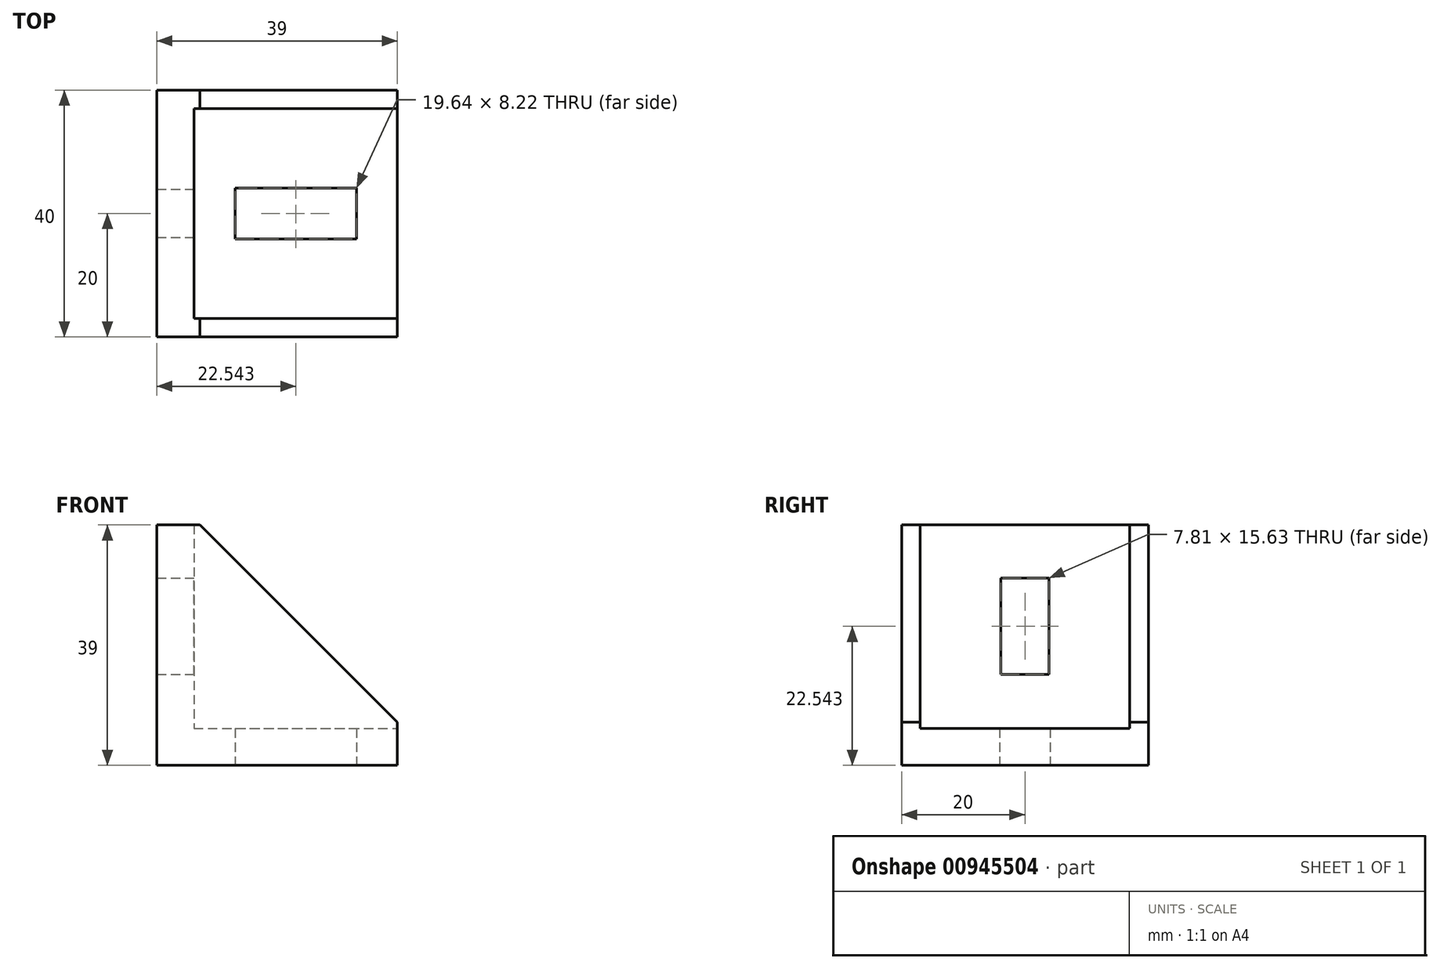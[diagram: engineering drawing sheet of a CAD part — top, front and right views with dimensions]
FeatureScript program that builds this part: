
annotation { "Feature Type Name" : "Feature", "Feature Type Description" : "" }
export const myFeature = defineFeature(function(context is Context, id is Id, definition is map)
    precondition{}
    {
        {
            var Q0;
            Q0=qCreatedBy(makeId("Front.planeOp"),FACE);
            var sketch = newSketch(context, id + "F0", { "sketchPlane" : qUnion([Q0])});
            skLineSegment(sketch, "E0.bottom", {"start": v(0, 0) * mm, "end": v(39, 0) * mm});
            skLineSegment(sketch, "E0.top", {"start": v(0, 39) * mm, "end": v(7, 39) * mm});
            skLineSegment(sketch, "E0.left", {"start": v(0, 0) * mm, "end": v(0, 39) * mm});
            skLineSegment(sketch, "E0.right", {"start": v(39, 0) * mm, "end": v(39, 7) * mm});
            skLineSegment(sketch, "E1", {"start": v(7, 39) * mm, "end": v(39, 7) * mm});
            skSolve(sketch);
        }
        {
            var Q0;
            Q0=makeQuery(id+"F0.imprint","IMPRINT",FACE,{"disambiguationData":[TD([[makeQuery(id+"F0.imprint","IMPRINT",EDGE,{"derivedFrom":sQuery(id+"F0.wireOp",EDGE,"E0.bottom")}),1.0]])]});
            extrude(context, id + "F1", {"entities" : qUnion([Q0]), "endBound" : BoundingType.SYMMETRIC, "depth" : 40 * mm, "offsetDistance" : 25 * mm});
        }
        {
            var Q0;
            Q0=qCreatedBy(makeId("Top.planeOp"),FACE);
            var sketch = newSketch(context, id + "F2", { "sketchPlane" : qUnion([Q0])});
            skLineSegment(sketch, "E2.bottom", {"start": v(6, 17) * mm, "end": v(39, 17) * mm});
            skLineSegment(sketch, "E2.top", {"start": v(6, -17) * mm, "end": v(39, -17) * mm});
            skLineSegment(sketch, "E2.left", {"start": v(6, 17) * mm, "end": v(6, -17) * mm});
            skLineSegment(sketch, "E2.right", {"start": v(39, 17) * mm, "end": v(39, -17) * mm});
            skSolve(sketch);
        }
        {
            var Q0;
            Q0=makeQuery(id+"F2.imprint","IMPRINT",FACE,{"disambiguationData":[TD([[makeQuery(id+"F2.imprint","IMPRINT",EDGE,{"derivedFrom":sQuery(id+"F2.wireOp",EDGE,"E2.bottom")}),-1.0]])]});
            extrude(context, id + "F3", {"entities" : qUnion([Q0]), "operationType" : NewBodyOperationType.REMOVE, "endBound" : BoundingType.THROUGH_ALL, "depth" : 25 * mm, "offsetDistance" : 25 * mm});
        }
        {
            var Q0;
            Q0 = qSketchRegion(id + "F2", true);
            extrude(context, id + "F4", {"entities" : qUnion([Q0]), "operationType" : NewBodyOperationType.ADD, "depth" : 6 * mm, "offsetDistance" : 25 * mm});
        }
        {
            var Q0;
            Q0=makeQuery(id+"F3.boolean.opBoolean","COPY",FACE,{"derivedFrom":makeQuery(id+"F3.opExtrude","SWEPT_FACE",FACE,{"disambiguationData":[OSD([sQuery(id+"F2.wireOp",EDGE,"E2.left")])]})});
            var sketch = newSketch(context, id + "F5", { "sketchPlane" : qUnion([Q0])});
            skLineSegment(sketch, "E3.bottom", {"start": v(3.9, 14.73) * mm, "end": v(-3.9, 14.73) * mm});
            skLineSegment(sketch, "E3.top", {"start": v(3.9, 30.36) * mm, "end": v(-3.9, 30.36) * mm});
            skLineSegment(sketch, "E3.left", {"start": v(3.9, 14.73) * mm, "end": v(3.9, 30.36) * mm});
            skLineSegment(sketch, "E3.right", {"start": v(-3.9, 14.73) * mm, "end": v(-3.9, 30.36) * mm});
            skPoint(sketch, "E3.middle", {"position": v(0, 22.54) * mm});
            skSolve(sketch);
        }
        {
            var Q0;
            Q0=makeQuery(id+"F5.imprint","IMPRINT",FACE,{"disambiguationData":[TD([[makeQuery(id+"F5.imprint","IMPRINT",EDGE,{"derivedFrom":sQuery(id+"F5.wireOp",EDGE,"E3.bottom")}),-1.0]])]});
            extrude(context, id + "F6", {"entities" : qUnion([Q0]), "operationType" : NewBodyOperationType.REMOVE, "oppositeDirection" : true, "depth" : 25 * mm, "offsetDistance" : 25 * mm});
        }
        {
            var Q0;
            Q0=qCreatedBy(makeId("Top.planeOp"),FACE);
            var sketch = newSketch(context, id + "F7", { "sketchPlane" : qUnion([Q0])});
            skLineSegment(sketch, "E4.bottom", {"start": v(32.36, -4.1) * mm, "end": v(12.72, -4.1) * mm});
            skLineSegment(sketch, "E4.top", {"start": v(32.36, 4.1) * mm, "end": v(12.72, 4.1) * mm});
            skLineSegment(sketch, "E4.left", {"start": v(32.36, -4.1) * mm, "end": v(32.36, 4.1) * mm});
            skLineSegment(sketch, "E4.right", {"start": v(12.72, -4.1) * mm, "end": v(12.72, 4.1) * mm});
            skPoint(sketch, "E4.middle", {"position": v(22.54, 0) * mm});
            skSolve(sketch);
        }
        {
            var Q0;
            Q0 = qSketchRegion(id + "F7", true);
            extrude(context, id + "F8", {"entities" : qUnion([Q0]), "operationType" : NewBodyOperationType.REMOVE, "endBound" : BoundingType.THROUGH_ALL, "depth" : 25 * mm, "offsetDistance" : 25 * mm});
        }
    });
